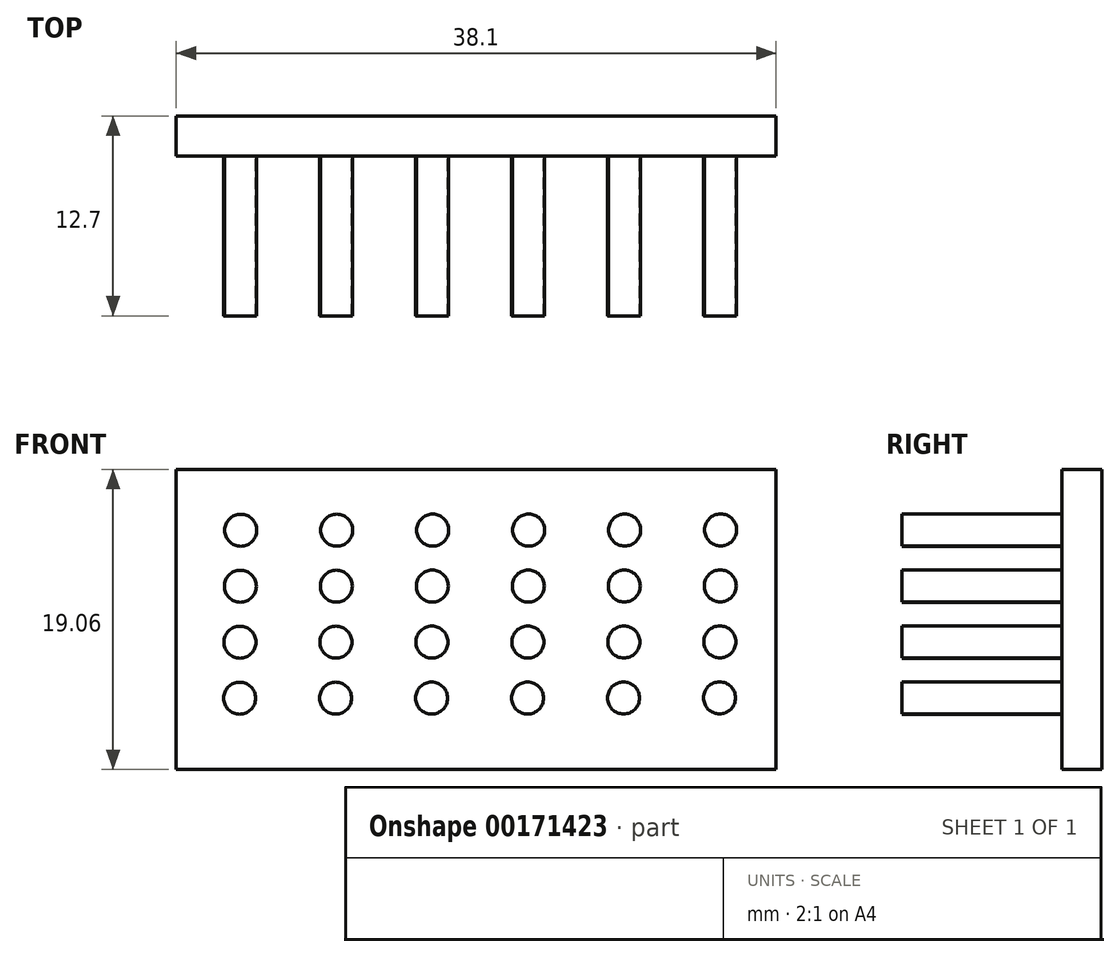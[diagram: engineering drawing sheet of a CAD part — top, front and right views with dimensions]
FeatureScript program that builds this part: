
annotation { "Feature Type Name" : "Feature", "Feature Type Description" : "" }
export const myFeature = defineFeature(function(context is Context, id is Id, definition is map)
    precondition{}
    {
        {
            var Q0;
            Q0=qCreatedBy(makeId("Front.planeOp"),FACE);
            var sketch = newSketch(context, id + "F0", { "sketchPlane" : qUnion([Q0])});
            skLineSegment(sketch, "E0.bottom", {"start": v(-19.05, 9.53) * mm, "end": v(19.05, 9.53) * mm});
            skLineSegment(sketch, "E0.top", {"start": v(-19.05, -9.52) * mm, "end": v(19.05, -9.52) * mm});
            skLineSegment(sketch, "E0.left", {"start": v(-19.05, 9.53) * mm, "end": v(-19.05, -9.52) * mm});
            skLineSegment(sketch, "E0.right", {"start": v(19.05, 9.53) * mm, "end": v(19.05, -9.52) * mm});
            skPoint(sketch, "E0.middle", {"position": v(0, 0) * mm});
            skSolve(sketch);
        }
        {
            var Q0;
            Q0=makeQuery(id+"F0.imprint","IMPRINT",FACE,{"disambiguationData":[TD([[makeQuery(id+"F0.imprint","IMPRINT",EDGE,{"derivedFrom":sQuery(id+"F0.wireOp",EDGE,"E0.bottom")}),-1.0]])]});
            extrude(context, id + "F1", {"entities" : qUnion([Q0]), "depth" : 2.54 * mm});
        }
        {
            var Q0;
            Q0=makeQuery(id+"F1.opExtrude","CAP_FACE",FACE,{"disambiguationData":[OSD([sQuery(id+"F0.wireOp",EDGE,"E0.bottom"),sQuery(id+"F0.wireOp",EDGE,"E0.top"),sQuery(id+"F0.wireOp",EDGE,"E0.left"),sQuery(id+"F0.wireOp",EDGE,"E0.right")])],"isStart":false});
            var sketch = newSketch(context, id + "F2", { "sketchPlane" : qUnion([Q0])});
            skCircle(sketch, "E1", {"center": v(-14.95, 5.67) * mm, "radius": 1.02 * mm});
            skCircle(sketch, "E2.0.1.0", {"center": v(-14.98, 2.11) * mm, "radius": 1.02 * mm});
            skCircle(sketch, "E2.0.2.0", {"center": v(-15, -1.44) * mm, "radius": 1.02 * mm});
            skCircle(sketch, "E2.0.3.0", {"center": v(-15.02, -5) * mm, "radius": 1.02 * mm});
            skCircle(sketch, "E2.1.0.0", {"center": v(-8.86, 5.67) * mm, "radius": 1.02 * mm});
            skCircle(sketch, "E2.1.1.0", {"center": v(-8.88, 2.12) * mm, "radius": 1.02 * mm});
            skCircle(sketch, "E2.1.2.0", {"center": v(-8.9, -1.44) * mm, "radius": 1.02 * mm});
            skCircle(sketch, "E2.1.3.0", {"center": v(-8.93, -5) * mm, "radius": 1.02 * mm});
            skCircle(sketch, "E2.2.0.0", {"center": v(-2.76, 5.68) * mm, "radius": 1.02 * mm});
            skCircle(sketch, "E2.2.1.0", {"center": v(-2.78, 2.12) * mm, "radius": 1.02 * mm});
            skCircle(sketch, "E2.2.2.0", {"center": v(-2.8, -1.44) * mm, "radius": 1.02 * mm});
            skCircle(sketch, "E2.2.3.0", {"center": v(-2.83, -5) * mm, "radius": 1.02 * mm});
            skCircle(sketch, "E2.3.0.0", {"center": v(3.34, 5.68) * mm, "radius": 1.02 * mm});
            skCircle(sketch, "E2.3.1.0", {"center": v(3.31, 2.12) * mm, "radius": 1.02 * mm});
            skCircle(sketch, "E2.3.2.0", {"center": v(3.29, -1.43) * mm, "radius": 1.02 * mm});
            skCircle(sketch, "E2.3.3.0", {"center": v(3.27, -4.99) * mm, "radius": 1.02 * mm});
            skCircle(sketch, "E2.4.0.0", {"center": v(9.43, 5.68) * mm, "radius": 1.02 * mm});
            skCircle(sketch, "E2.4.1.0", {"center": v(9.4, 2.13) * mm, "radius": 1.02 * mm});
            skCircle(sketch, "E2.4.2.0", {"center": v(9.39, -1.43) * mm, "radius": 1.02 * mm});
            skCircle(sketch, "E2.4.3.0", {"center": v(9.36, -4.98) * mm, "radius": 1.02 * mm});
            skCircle(sketch, "E2.5.0.0", {"center": v(15.53, 5.69) * mm, "radius": 1.02 * mm});
            skCircle(sketch, "E2.5.1.0", {"center": v(15.5, 2.13) * mm, "radius": 1.02 * mm});
            skCircle(sketch, "E2.5.2.0", {"center": v(15.48, -1.42) * mm, "radius": 1.02 * mm});
            skCircle(sketch, "E2.5.3.0", {"center": v(15.46, -4.98) * mm, "radius": 1.02 * mm});
            skLineSegment(sketch, "E2.direction1", {"start": v(-14.95, 5.67) * mm, "end": v(-8.86, 5.67) * mm, "construction": true});
            skLineSegment(sketch, "E2.direction2", {"start": v(-14.95, 5.67) * mm, "end": v(-14.98, 2.11) * mm, "construction": true});
            skSolve(sketch);
        }
        {
            var Q0;
            Q0=makeQuery(id+"F2.imprint","IMPRINT",FACE,{"disambiguationData":[TD([[makeQuery(id+"F2.imprint","IMPRINT",EDGE,{"derivedFrom":sQuery(id+"F2.wireOp",EDGE,"E1")}),1.0]])]});
            var Q1;
            Q1=makeQuery(id+"F2.imprint","IMPRINT",FACE,{"disambiguationData":[TD([[makeQuery(id+"F2.imprint","IMPRINT",EDGE,{"derivedFrom":sQuery(id+"F2.wireOp",EDGE,"E2.1.0.0")}),1.0]])]});
            var Q2;
            Q2=makeQuery(id+"F2.imprint","IMPRINT",FACE,{"disambiguationData":[TD([[makeQuery(id+"F2.imprint","IMPRINT",EDGE,{"derivedFrom":sQuery(id+"F2.wireOp",EDGE,"E2.1.1.0")}),1.0]])]});
            var Q3;
            Q3=makeQuery(id+"F2.imprint","IMPRINT",FACE,{"disambiguationData":[TD([[makeQuery(id+"F2.imprint","IMPRINT",EDGE,{"derivedFrom":sQuery(id+"F2.wireOp",EDGE,"E2.0.1.0")}),1.0]])]});
            var Q4;
            Q4=makeQuery(id+"F2.imprint","IMPRINT",FACE,{"disambiguationData":[TD([[makeQuery(id+"F2.imprint","IMPRINT",EDGE,{"derivedFrom":sQuery(id+"F2.wireOp",EDGE,"E2.0.2.0")}),1.0]])]});
            var Q5;
            Q5=makeQuery(id+"F2.imprint","IMPRINT",FACE,{"disambiguationData":[TD([[makeQuery(id+"F2.imprint","IMPRINT",EDGE,{"derivedFrom":sQuery(id+"F2.wireOp",EDGE,"E2.1.2.0")}),1.0]])]});
            var Q6;
            Q6=makeQuery(id+"F2.imprint","IMPRINT",FACE,{"disambiguationData":[TD([[makeQuery(id+"F2.imprint","IMPRINT",EDGE,{"derivedFrom":sQuery(id+"F2.wireOp",EDGE,"E2.1.3.0")}),1.0]])]});
            var Q7;
            Q7=makeQuery(id+"F2.imprint","IMPRINT",FACE,{"disambiguationData":[TD([[makeQuery(id+"F2.imprint","IMPRINT",EDGE,{"derivedFrom":sQuery(id+"F2.wireOp",EDGE,"E2.0.3.0")}),1.0]])]});
            var Q8;
            Q8=makeQuery(id+"F2.imprint","IMPRINT",FACE,{"disambiguationData":[TD([[makeQuery(id+"F2.imprint","IMPRINT",EDGE,{"derivedFrom":sQuery(id+"F2.wireOp",EDGE,"E2.0.4.0")}),1.0]])]});
            var Q9;
            Q9=makeQuery(id+"F2.imprint","IMPRINT",FACE,{"disambiguationData":[TD([[makeQuery(id+"F2.imprint","IMPRINT",EDGE,{"derivedFrom":sQuery(id+"F2.wireOp",EDGE,"E2.1.4.0")}),1.0]])]});
            var Q10;
            Q10=makeQuery(id+"F2.imprint","IMPRINT",FACE,{"disambiguationData":[TD([[makeQuery(id+"F2.imprint","IMPRINT",EDGE,{"derivedFrom":sQuery(id+"F2.wireOp",EDGE,"E2.1.5.0")}),1.0]])]});
            var Q11;
            Q11=makeQuery(id+"F2.imprint","IMPRINT",FACE,{"disambiguationData":[TD([[makeQuery(id+"F2.imprint","IMPRINT",EDGE,{"derivedFrom":sQuery(id+"F2.wireOp",EDGE,"E2.0.5.0")}),1.0]])]});
            var Q12;
            Q12=makeQuery(id+"F2.imprint","IMPRINT",FACE,{"disambiguationData":[TD([[makeQuery(id+"F2.imprint","IMPRINT",EDGE,{"derivedFrom":sQuery(id+"F2.wireOp",EDGE,"E2.2.5.0")}),1.0]])]});
            var Q13;
            Q13=makeQuery(id+"F2.imprint","IMPRINT",FACE,{"disambiguationData":[TD([[makeQuery(id+"F2.imprint","IMPRINT",EDGE,{"derivedFrom":sQuery(id+"F2.wireOp",EDGE,"E2.2.4.0")}),1.0]])]});
            var Q14;
            Q14=makeQuery(id+"F2.imprint","IMPRINT",FACE,{"disambiguationData":[TD([[makeQuery(id+"F2.imprint","IMPRINT",EDGE,{"derivedFrom":sQuery(id+"F2.wireOp",EDGE,"E2.2.3.0")}),1.0]])]});
            var Q15;
            Q15=makeQuery(id+"F2.imprint","IMPRINT",FACE,{"disambiguationData":[TD([[makeQuery(id+"F2.imprint","IMPRINT",EDGE,{"derivedFrom":sQuery(id+"F2.wireOp",EDGE,"E2.2.2.0")}),1.0]])]});
            var Q16;
            Q16=makeQuery(id+"F2.imprint","IMPRINT",FACE,{"disambiguationData":[TD([[makeQuery(id+"F2.imprint","IMPRINT",EDGE,{"derivedFrom":sQuery(id+"F2.wireOp",EDGE,"E2.2.1.0")}),1.0]])]});
            var Q17;
            Q17=makeQuery(id+"F2.imprint","IMPRINT",FACE,{"disambiguationData":[TD([[makeQuery(id+"F2.imprint","IMPRINT",EDGE,{"derivedFrom":sQuery(id+"F2.wireOp",EDGE,"E2.2.0.0")}),1.0]])]});
            var Q18;
            Q18=makeQuery(id+"F2.imprint","IMPRINT",FACE,{"disambiguationData":[TD([[makeQuery(id+"F2.imprint","IMPRINT",EDGE,{"derivedFrom":sQuery(id+"F2.wireOp",EDGE,"E2.3.0.0")}),1.0]])]});
            var Q19;
            Q19=makeQuery(id+"F2.imprint","IMPRINT",FACE,{"disambiguationData":[TD([[makeQuery(id+"F2.imprint","IMPRINT",EDGE,{"derivedFrom":sQuery(id+"F2.wireOp",EDGE,"E2.3.1.0")}),1.0]])]});
            var Q20;
            Q20=makeQuery(id+"F2.imprint","IMPRINT",FACE,{"disambiguationData":[TD([[makeQuery(id+"F2.imprint","IMPRINT",EDGE,{"derivedFrom":sQuery(id+"F2.wireOp",EDGE,"E2.3.2.0")}),1.0]])]});
            var Q21;
            Q21=makeQuery(id+"F2.imprint","IMPRINT",FACE,{"disambiguationData":[TD([[makeQuery(id+"F2.imprint","IMPRINT",EDGE,{"derivedFrom":sQuery(id+"F2.wireOp",EDGE,"E2.3.3.0")}),1.0]])]});
            var Q22;
            Q22=makeQuery(id+"F2.imprint","IMPRINT",FACE,{"disambiguationData":[TD([[makeQuery(id+"F2.imprint","IMPRINT",EDGE,{"derivedFrom":sQuery(id+"F2.wireOp",EDGE,"E2.3.4.0")}),1.0]])]});
            var Q23;
            Q23=makeQuery(id+"F2.imprint","IMPRINT",FACE,{"disambiguationData":[TD([[makeQuery(id+"F2.imprint","IMPRINT",EDGE,{"derivedFrom":sQuery(id+"F2.wireOp",EDGE,"E2.3.5.0")}),1.0]])]});
            extrude(context, id + "F3", {"entities" : qUnion([Q0, Q1, Q2, Q3, Q4, Q5, Q6, Q7, Q8, Q9, Q10, Q11, Q12, Q13, Q14, Q15, Q16, Q17, Q18, Q19, Q20, Q21, Q22, Q23]), "operationType" : NewBodyOperationType.ADD, "depth" : 10.16 * mm});
        }
        {
            var Q0;
            Q0=makeQuery(id+"F2.imprint","IMPRINT",FACE,{"disambiguationData":[TD([[makeQuery(id+"F2.imprint","IMPRINT",EDGE,{"derivedFrom":sQuery(id+"F2.wireOp",EDGE,"E2.4.0.0")}),1.0]])]});
            var Q1;
            Q1=makeQuery(id+"F2.imprint","IMPRINT",FACE,{"disambiguationData":[TD([[makeQuery(id+"F2.imprint","IMPRINT",EDGE,{"derivedFrom":sQuery(id+"F2.wireOp",EDGE,"E2.4.1.0")}),1.0]])]});
            var Q2;
            Q2=makeQuery(id+"F2.imprint","IMPRINT",FACE,{"disambiguationData":[TD([[makeQuery(id+"F2.imprint","IMPRINT",EDGE,{"derivedFrom":sQuery(id+"F2.wireOp",EDGE,"E2.4.2.0")}),1.0]])]});
            var Q3;
            Q3=makeQuery(id+"F2.imprint","IMPRINT",FACE,{"disambiguationData":[TD([[makeQuery(id+"F2.imprint","IMPRINT",EDGE,{"derivedFrom":sQuery(id+"F2.wireOp",EDGE,"E2.4.3.0")}),1.0]])]});
            var Q4;
            Q4=makeQuery(id+"F2.imprint","IMPRINT",FACE,{"disambiguationData":[TD([[makeQuery(id+"F2.imprint","IMPRINT",EDGE,{"derivedFrom":sQuery(id+"F2.wireOp",EDGE,"E2.4.4.0")}),1.0]])]});
            var Q5;
            Q5=makeQuery(id+"F2.imprint","IMPRINT",FACE,{"disambiguationData":[TD([[makeQuery(id+"F2.imprint","IMPRINT",EDGE,{"derivedFrom":sQuery(id+"F2.wireOp",EDGE,"E2.4.5.0")}),1.0]])]});
            var Q6;
            Q6=makeQuery(id+"F2.imprint","IMPRINT",FACE,{"disambiguationData":[TD([[makeQuery(id+"F2.imprint","IMPRINT",EDGE,{"derivedFrom":sQuery(id+"F2.wireOp",EDGE,"E2.5.5.0")}),1.0]])]});
            var Q7;
            Q7=makeQuery(id+"F2.imprint","IMPRINT",FACE,{"disambiguationData":[TD([[makeQuery(id+"F2.imprint","IMPRINT",EDGE,{"derivedFrom":sQuery(id+"F2.wireOp",EDGE,"E2.5.4.0")}),1.0]])]});
            var Q8;
            Q8=makeQuery(id+"F2.imprint","IMPRINT",FACE,{"disambiguationData":[TD([[makeQuery(id+"F2.imprint","IMPRINT",EDGE,{"derivedFrom":sQuery(id+"F2.wireOp",EDGE,"E2.5.3.0")}),1.0]])]});
            var Q9;
            Q9=makeQuery(id+"F2.imprint","IMPRINT",FACE,{"disambiguationData":[TD([[makeQuery(id+"F2.imprint","IMPRINT",EDGE,{"derivedFrom":sQuery(id+"F2.wireOp",EDGE,"E2.5.2.0")}),1.0]])]});
            var Q10;
            Q10=makeQuery(id+"F2.imprint","IMPRINT",FACE,{"disambiguationData":[TD([[makeQuery(id+"F2.imprint","IMPRINT",EDGE,{"derivedFrom":sQuery(id+"F2.wireOp",EDGE,"E2.5.1.0")}),1.0]])]});
            var Q11;
            Q11=makeQuery(id+"F2.imprint","IMPRINT",FACE,{"disambiguationData":[TD([[makeQuery(id+"F2.imprint","IMPRINT",EDGE,{"derivedFrom":sQuery(id+"F2.wireOp",EDGE,"E2.5.0.0")}),1.0]])]});
            var Q12;
            Q12=makeQuery(id+"F2.imprint","IMPRINT",FACE,{"disambiguationData":[TD([[makeQuery(id+"F2.imprint","IMPRINT",EDGE,{"derivedFrom":sQuery(id+"F2.wireOp",EDGE,"E2.6.0.0")}),1.0]])]});
            var Q13;
            Q13=makeQuery(id+"F2.imprint","IMPRINT",FACE,{"disambiguationData":[TD([[makeQuery(id+"F2.imprint","IMPRINT",EDGE,{"derivedFrom":sQuery(id+"F2.wireOp",EDGE,"E2.6.1.0")}),1.0]])]});
            var Q14;
            Q14=makeQuery(id+"F2.imprint","IMPRINT",FACE,{"disambiguationData":[TD([[makeQuery(id+"F2.imprint","IMPRINT",EDGE,{"derivedFrom":sQuery(id+"F2.wireOp",EDGE,"E2.6.2.0")}),1.0]])]});
            var Q15;
            Q15=makeQuery(id+"F2.imprint","IMPRINT",FACE,{"disambiguationData":[TD([[makeQuery(id+"F2.imprint","IMPRINT",EDGE,{"derivedFrom":sQuery(id+"F2.wireOp",EDGE,"E2.6.3.0")}),1.0]])]});
            var Q16;
            Q16=makeQuery(id+"F2.imprint","IMPRINT",FACE,{"disambiguationData":[TD([[makeQuery(id+"F2.imprint","IMPRINT",EDGE,{"derivedFrom":sQuery(id+"F2.wireOp",EDGE,"E2.6.4.0")}),1.0]])]});
            var Q17;
            Q17=makeQuery(id+"F2.imprint","IMPRINT",FACE,{"disambiguationData":[TD([[makeQuery(id+"F2.imprint","IMPRINT",EDGE,{"derivedFrom":sQuery(id+"F2.wireOp",EDGE,"E2.6.5.0")}),1.0]])]});
            var Q18;
            Q18=makeQuery(id+"F2.imprint","IMPRINT",FACE,{"disambiguationData":[TD([[makeQuery(id+"F2.imprint","IMPRINT",EDGE,{"derivedFrom":sQuery(id+"F2.wireOp",EDGE,"E2.7.5.0")}),1.0]])]});
            var Q19;
            Q19=makeQuery(id+"F2.imprint","IMPRINT",FACE,{"disambiguationData":[TD([[makeQuery(id+"F2.imprint","IMPRINT",EDGE,{"derivedFrom":sQuery(id+"F2.wireOp",EDGE,"E2.7.4.0")}),1.0]])]});
            var Q20;
            Q20=makeQuery(id+"F2.imprint","IMPRINT",FACE,{"disambiguationData":[TD([[makeQuery(id+"F2.imprint","IMPRINT",EDGE,{"derivedFrom":sQuery(id+"F2.wireOp",EDGE,"E2.7.3.0")}),1.0]])]});
            var Q21;
            Q21=makeQuery(id+"F2.imprint","IMPRINT",FACE,{"disambiguationData":[TD([[makeQuery(id+"F2.imprint","IMPRINT",EDGE,{"derivedFrom":sQuery(id+"F2.wireOp",EDGE,"E2.7.2.0")}),1.0]])]});
            var Q22;
            Q22=makeQuery(id+"F2.imprint","IMPRINT",FACE,{"disambiguationData":[TD([[makeQuery(id+"F2.imprint","IMPRINT",EDGE,{"derivedFrom":sQuery(id+"F2.wireOp",EDGE,"E2.7.1.0")}),1.0]])]});
            var Q23;
            Q23=makeQuery(id+"F2.imprint","IMPRINT",FACE,{"disambiguationData":[TD([[makeQuery(id+"F2.imprint","IMPRINT",EDGE,{"derivedFrom":sQuery(id+"F2.wireOp",EDGE,"E2.7.0.0")}),1.0]])]});
            extrude(context, id + "F4", {"entities" : qUnion([Q0, Q1, Q2, Q3, Q4, Q5, Q6, Q7, Q8, Q9, Q10, Q11, Q12, Q13, Q14, Q15, Q16, Q17, Q18, Q19, Q20, Q21, Q22, Q23]), "operationType" : NewBodyOperationType.ADD, "depth" : 10.16 * mm});
        }
    });
